# Revit family: Pump_Commercial-Effluent-Zoeller-6180_Series (1)
name_source: partatom
category: Mechanical Equipment
revit_build: Autodesk Revit 2018 (Build: 20170223_1515(x64)
units: mm (PartAtom-declared; Revit-internal decimal feet)

## family parameters
Always vertical = No
Cut with Voids When Loaded = No
OmniClass Number = 23.60.30.21
OmniClass Title = Pumps
Part Type = Normal
Room Calculation Point = No
Round Connector Dimension = Use Radius
Shared = Yes
Work Plane-Based = Yes

## types (12) — shared parameters
Assembly Code = D2010900
Default Elevation = 0"
Description = Commercial Effluent Pumps
Discharge Height = 6"
Height = 21 3/16"
Hertz = 60
Impeller = Cast Iron
Impeller Type = Vortex
Installation Type = Floor Mounted
Length = 12 3/4"
Manufacturer = Zoeller
Masterformat Number = 33 36 16
Masterformat Title = Utility Septic Tank Effluent Pumps
Material = Cast Iron-Zoeller-Powder Coated Epoxy
Max. Water Temp. = 130 °F
Min. Recommended Fluid Level = 10"
Moisture Sensor (Optional) = Requires a circuit in control panel
Motor Design Letter = NEMA B
Motor Shaft = 416 S.S.
Motor Thermal Shutoff (Single Phase Only) = Thermal Overload Sensors With Automatic Reset.
Motor Type = Submersible
O-Rings and Cover Gasket = Viton
Omniclass Table 23 Code = 23.60.30.21
Omniclass Table 23 Title = Pumps
Operation = Non-Automatic
Phase = 1 or 3
Price = Prices may vary. Please consult Manufacturer Representative for most up-to-date price list.
Product Page URL = http://www.zoellerengprod.com
RPM = 3450
Service Factor = 1.15
Shaft Seal Lower (Options) = Silicon Carbide/Silicon Carbide
Shaft Seal Lower Standard = Silicon Carbide/Carbon
Shaft Seal Upper (Options) = Silicon Carbide/Carbon, Silicon Carbide/Silicon Carbide
Shaft Seal Upper Standard = Carbon/Ceramic
Shipping Weight = 89-94 lbs
Type = Permanent Split Capacitor or 3 Phase
Type SOW Power Cord Length = 300"
URL = http://www.zoellerengprod.com
Warranty Information = 36 Months (Limited)
Waste Connection = Yes
Width = 8"

## per-type parameters (varying)
| type | Discharge Diameter | Discharge Radius | Flange | Flange Visibility Height | Full Load Amps (Voltage Dependent) | Insulation | Lead Wires Insulation | Locked Rotor Amps (Voltage Dependant) | Max. Flow at Min. Head | Max. Stator Temp. | Maximum Head | Minimum Head | Motor | No Flange | Void Visibility | Voltage |
| 6185-1.5" | 1-1/2" NPT | 3/4" | No | 5 1/2" | 3.3-11.5 | Class B | Class B | 12-30 | 85 GPM @ 5' | 266 °F | 876" | 360" | 1 HP | Yes | 8 1/4" | 115-575 |
| 6186-1.5" | 1-1/2" NPT | 3/4" | No | 5 1/2" | 4.6-17.2 | Class F | Class F | 18-48.3 | 58 GPM @ 5' | 311 °F | 1368" | 60" | 1-1/2 HP | Yes | 8 1/4" | 115-460 |
| 6185-2" | 2" NPT | 1" | Yes | 6" | 3.3-11.5 | Class B | Class B | 12-30 | 85 GPM @ 5' | 266 °F | 876" | 360" | 1 HP | No | 3" | 115-575 |
| 6185-3" | 3" NPT | 1 1/2" | Yes | 6" | 3.3-11.5 | Class B | Class B | 12-30 | 85 GPM @ 5' | 266 °F | 876" | 360" | 1 HP | No | 3" | 115-575 |
| 6186-2" | 2" NPT | 1" | Yes | 6" | 4.6-17.2 | Class F | Class F | 18-48.3 | 58 GPM @ 5' | 311 °F | 1368" | 60" | 1-1/2 HP | No | 3" | 115-460 |
| 6186-3" | 3" NPT | 1 1/2" | Yes | 6" | 4.6-17.2 | Class F | Class F | 18-48.3 | 58 GPM @ 5' | 311 °F | 1368" | 60" | 1-1/2 HP | No | 3" | 115-460 |
| 6188-1.5" | 1-1/2" NPT | 3/4" | No | 5 1/2" | 3.5-16.8 | Class F | Class F | 18-48.3 | 145 GPM @ 5' | 311 °F | 1092" | 60" | 1-1/2 HP | Yes | 8 1/4" | 115-575 |
| 6188-2" | 2" NPT | 1" | Yes | 6" | 3.5-16.8 | Class F | Class F | 18-48.3 | 145 GPM @ 5' | 311 °F | 1092" | 60" | 1-1/2 HP | No | 3" | 115-575 |
| 6188-3" | 3" NPT | 1 1/2" | Yes | 6" | 3.5-16.8 | Class F | Class F | 18-48.3 | 145 GPM @ 5' | 311 °F | 1092" | 60" | 1-1/2 HP | No | 3" | 115-575 |
| 6189-1.5" | 1-1/2" NPT | 3/4" | No | 5 1/2" | 5.8-20.5 | Class F | Class F | 18-48.3 | 145 GPM @ 5' | 266 °F | 1320" | 60" | 1 HP | Yes | 8 1/4" | 115-575 |
| 6189-2" | 2" NPT | 1" | Yes | 6" | 5.8-20.5 | Class F | Class F | 18-48.3 | 145 GPM @ 5' | 266 °F | 1320" | 60" | 1 HP | No | 3" | 115-575 |
| 6189-3" | 3" NPT | 1 1/2" | Yes | 6" | 5.8-20.5 | Class F | Class F | 18-48.3 | 145 GPM @ 5' | 266 °F | 1320" | 60" | 1 HP | No | 3" | 115-575 |

note: column(s) folded — value = type name in every type: Model

## geometry (parser evidence)
native form markers: Sweep x2
no freeform markers — native parametric forms only
